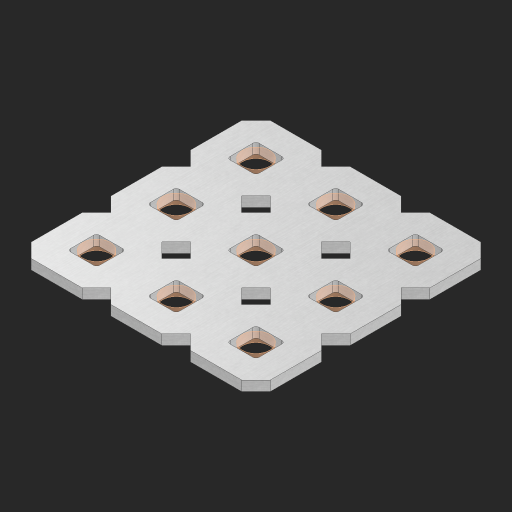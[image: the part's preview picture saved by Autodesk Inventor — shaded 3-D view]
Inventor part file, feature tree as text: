
AUTODESK INVENTOR PART (.ipt)
format: ipt  version: 2023 (Build 270158000, 158)  size: 403,456 bytes
history: native  units: in
note: dims shown in document units (in); Inventor stores cm internally (conversion verified against a paired STEP export)
features: other x10, extrude x8, sketch x2, pattern_linear x1
ambient origin geometry x8: Origin, YZ Plane, XZ Plane, XY Plane, X Axis, Y Axis, Z Axis, Center Point
bodies: Solid1 (feature_tree), Body (feature_tree)
feature tree (21):
  pattern_linear  "Rectangular Pattern1"  Spacing1=0.09in  [1 undecoded]
  sketch  "Sketch1"  dims[d1=0.5in]
  sketch  "Sketch2"  dims[d2=0.182in d3=0.09in d4=0.09in d5=0.09in d6=0.09in d7=0.09in d8=0.09in d9=0.09in d10=0.09in d11=0.02in d13=0.0in d14=0.172in d15=0.0625in d16=0.0in d19=0.5in d22=0.5in]
  other  "Srf1"
  other  "Srf126"
  other  "Srf127"
  other  "Srf268"
  other  "Srf269"
  other  "Srf270"
  other  "Srf293"
  other  "Srf294"
  other  "Srf295"
  other  "Circle"
  extrude  "ExtrusionSrf126"  Depth=0.09in
  extrude  "ExtrusionSrf127"  Depth=0.09in
  extrude  "ExtrusionSrf268"  Depth=0.09in
  extrude  "ExtrusionSrf269"  Depth=0.09in
  extrude  "ExtrusionSrf270"  Depth=0.09in
  extrude  "ExtrusionSrf293"  Depth=0.09in
  extrude  "ExtrusionSrf294"  Depth=0.09in
  extrude  "ExtrusionSrf295"  Depth=0.02in
note: 1 required parameter value undecoded (feature->parameter linkage not recoverable at this tier; creation-order binding heuristic only, values carry confidence <= 0.55)
